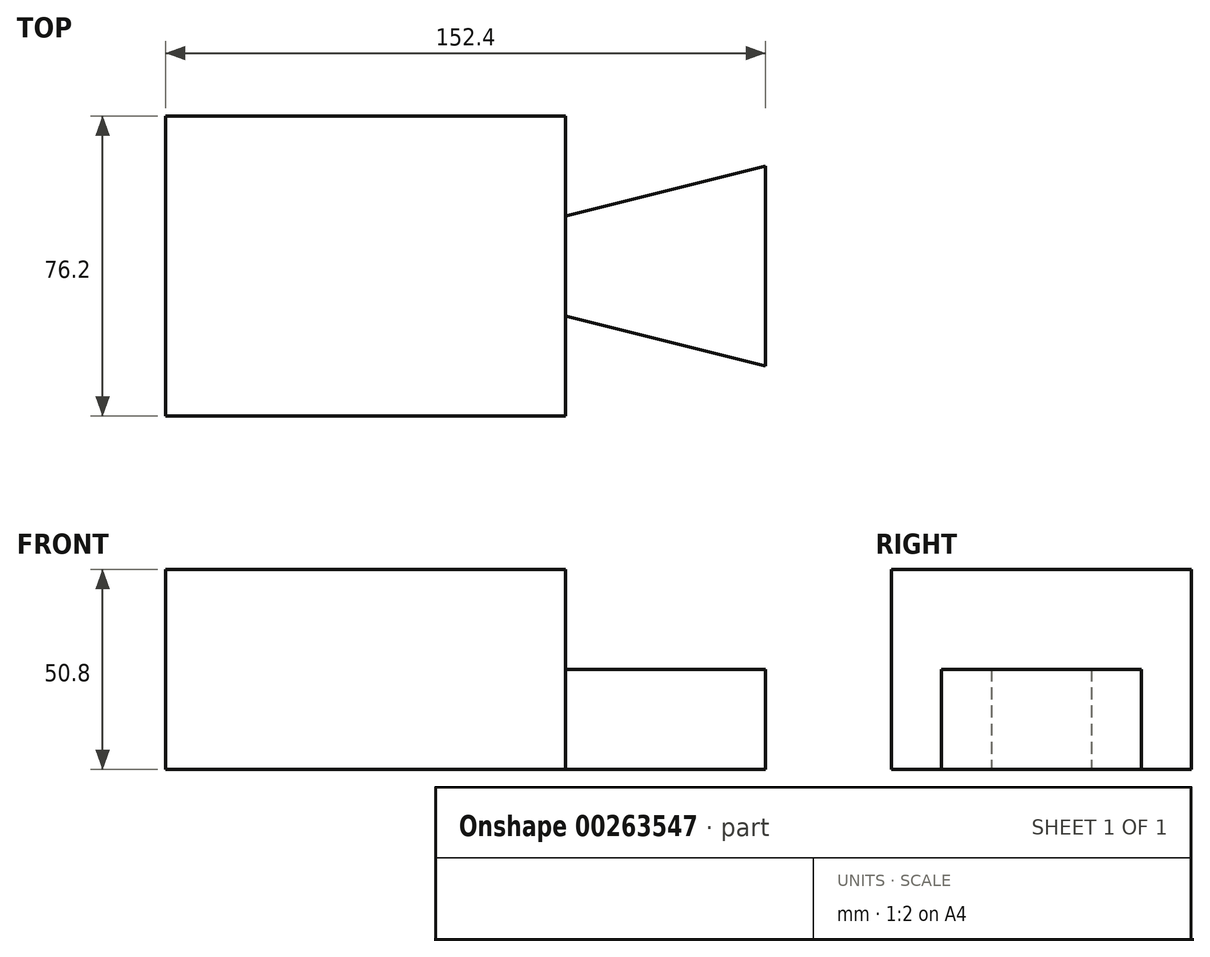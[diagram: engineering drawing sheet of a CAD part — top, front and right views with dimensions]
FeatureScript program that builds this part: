
annotation { "Feature Type Name" : "Feature", "Feature Type Description" : "" }
export const myFeature = defineFeature(function(context is Context, id is Id, definition is map)
    precondition{}
    {
        {
            var Q0;
            Q0=qCreatedBy(makeId("Front.planeOp"),FACE);
            var sketch = newSketch(context, id + "F0", { "sketchPlane" : qUnion([Q0])});
            skLineSegment(sketch, "E0", {"start": v(-71.38, -38.57) * mm, "end": v(30.22, -38.57) * mm});
            skLineSegment(sketch, "E1", {"start": v(-71.38, -38.57) * mm, "end": v(-71.38, 12.23) * mm});
            skLineSegment(sketch, "E2", {"start": v(-71.38, 12.23) * mm, "end": v(30.22, 12.23) * mm});
            skLineSegment(sketch, "E3", {"start": v(30.22, -38.57) * mm, "end": v(30.22, 12.23) * mm});
            skSolve(sketch);
        }
        {
            var Q0;
            Q0=makeQuery(id+"F0.imprint","IMPRINT",FACE,{"disambiguationData":[TD([[makeQuery(id+"F0.imprint","IMPRINT",EDGE,{"derivedFrom":sQuery(id+"F0.wireOp",EDGE,"E0")}),1.0]])]});
            extrude(context, id + "F1", {"entities" : qUnion([Q0]), "depth" : 76.2 * mm});
        }
        {
            var Q0;
            Q0=makeQuery(id+"F1.opExtrude","SWEPT_FACE",FACE,{"disambiguationData":[OSD([sQuery(id+"F0.wireOp",EDGE,"E0")])]});
            var sketch = newSketch(context, id + "F2", { "sketchPlane" : qUnion([Q0])});
            skLineSegment(sketch, "E4", {"start": v(30.22, 76.2) * mm, "end": v(30.22, 50.8) * mm});
            skLineSegment(sketch, "E5", {"start": v(30.22, 0) * mm, "end": v(30.22, 25.4) * mm});
            skLineSegment(sketch, "E6", {"start": v(81.02, 63.5) * mm, "end": v(81.02, 12.7) * mm});
            skLineSegment(sketch, "E7", {"start": v(81.02, 63.5) * mm, "end": v(30.22, 50.8) * mm});
            skLineSegment(sketch, "E8", {"start": v(81.02, 12.7) * mm, "end": v(30.22, 25.4) * mm});
            skPoint(sketch, "E9.start.orphan", {"position": v(30.22, 63.5) * mm});
            skPoint(sketch, "E10.end.orphan", {"position": v(30.22, 12.7) * mm});
            skSolve(sketch);
        }
        {
            var Q0;
            Q0=makeQuery(id+"F2.imprint","IMPRINT",FACE,{"disambiguationData":[TD([[makeQuery(id+"F2.imprint","IMPRINT",EDGE,{"derivedFrom":sQuery(id+"F2.wireOp",EDGE,"E6")}),-1.0]])]});
            extrude(context, id + "F3", {"entities" : qUnion([Q0]), "operationType" : NewBodyOperationType.ADD, "oppositeDirection" : true, "depth" : 25.4 * mm});
        }
    });
